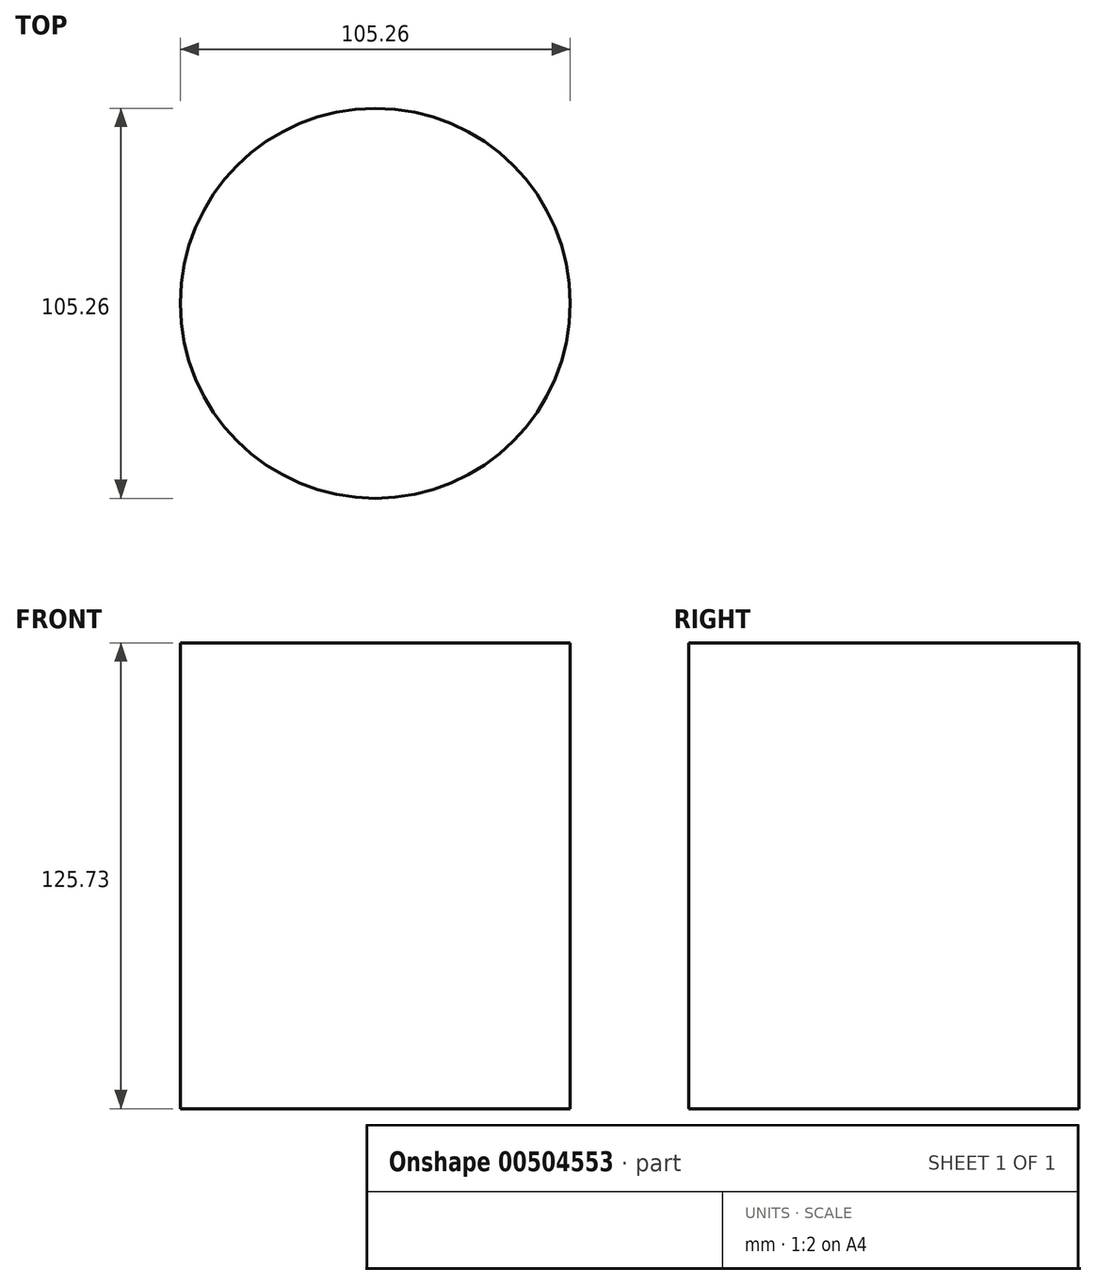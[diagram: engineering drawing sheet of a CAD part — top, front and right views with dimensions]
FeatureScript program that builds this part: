
annotation { "Feature Type Name" : "Feature", "Feature Type Description" : "" }
export const myFeature = defineFeature(function(context is Context, id is Id, definition is map)
    precondition{}
    {
        {
            var Q0;
            Q0=qCreatedBy(makeId("Top.planeOp"),FACE);
            var sketch = newSketch(context, id + "F0", { "sketchPlane" : qUnion([Q0])});
            skCircle(sketch, "E0", {"center": v(0, 0) * mm, "radius": 52.63 * mm});
            skSolve(sketch);
        }
        {
            var Q0;
            Q0=makeQuery(id+"F0.imprint","IMPRINT",FACE,{"disambiguationData":[TD([[makeQuery(id+"F0.imprint","IMPRINT",EDGE,{"derivedFrom":sQuery(id+"F0.wireOp",EDGE,"E0")}),1.0]])]});
            extrude(context, id + "F1", {"entities" : qUnion([Q0]), "depth" : 125.73 * mm});
        }
    });
